# Revit family: _Camera-Security-Panasonic-360-degree-Indoor-Dome-Network-S4151
name_source: partatom
category: Security Devices
units: mm (PartAtom-declared; Revit-internal decimal feet)

## family parameters
Cut with Voids When Loaded = No
Host = Face
Maintain Annotation Orientation = No
OmniClass Number = 23.85.10.14.11
OmniClass Title = Cameras
Part Type = Normal
Room Calculation Point = No
Round Connector Dimension = Use Diameter
Shared = No

## types (2) — shared parameters
Alarm Input Or Output Specification = ALARM IN 1 (Auto time adjustment) (x1),ALARM IN 2 (ALARM OUT) (x1), ALARM IN 3 (AUX OUT) (x1)
Angle Of View = 180
Audio In = Yes
Audio Out = Yes
Communication Ports = 10Base-T / 100Base-TX, RJ45 connector
Day Or Night = Yes
Equipment Abbreviation = SC
Family Version = 1.0.0
Focal Length = 0.033 "
Has POE = Yes
Height_Offset5 = 1.447 "
IP Or Analog = IP
Indoor Or Outdoor = Indoor
Manufacturer = Panasonic
Minimum Illumination = 0 lx
Model Disclaimer = Contact Panasonic for more information
Mounting Positions = Mount Dependent or Surface Mount
Operational Humidity = 10% to 90% (no condensation)
Power Active = 4.6 W
Product Material = Paint - Panasonic - Sail White
Product Page URL = https://security.panasonic.com
Provide Feedback = https://www.surveymonkey.com
Regulatory Compliance = UL UL60950-1, C-UL CAN/CSA C22.2 No.60950-1, CE, IEC60950-1 FCC Part15 ClassA, ICES003 ClassA, EN55022 ClassB, EN55024
Scanning Area H = 0.14 "
Scanning Area V = 0.14 "
Storage Temperature = -22 °F to 140 °F
URL = http://security.panasonic.com
Vandal Resistant = No
Voltage DC = 12 V
Wide Dynamic Range = Yes
z Base Raduius = 3.228 "
z Horizontal FOV = 186.00°
z Vertical FOV = 186.00°
zero-valued in all types: Default Elevation, z Base Height

## per-type parameters (varying)
| type | Date Last Modified | Description | Part Description | Product Documentation Link |
| WV-S4150 | November, 09, 2017 | Security Camera, 360-degree, Indoor, Dome, 5 Megapixel, Network, S4150 | Security Camera, 360-degree, Indoor, Dome, 5 Megapixel, Network, S4150 | http://ssbu-t.psn-web.net |
| WV-S4151 | October, 28, 2020 | Security Camera, 360-degree, Indoor, Dome, 5 Megapixel, Network, S4151 | Security Camera, 360-degree, Indoor, Dome, 5 Megapixel, Network, S4151 | https://bizpartner.panasonic.net |

note: column(s) folded — value = type name in every type: Model, Part Number

## geometry (parser evidence)
native form markers: Blend x2, Sweep x4
no freeform markers — native parametric forms only
